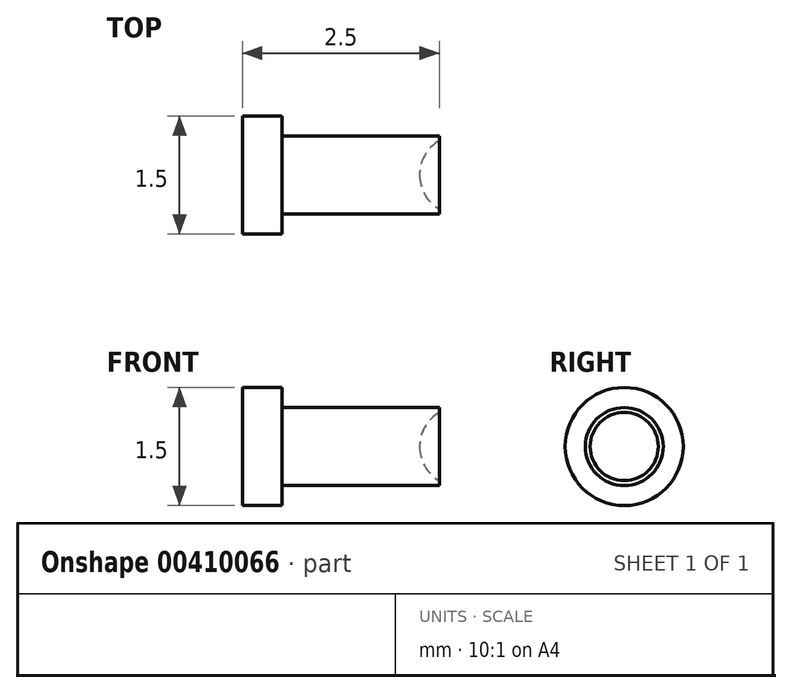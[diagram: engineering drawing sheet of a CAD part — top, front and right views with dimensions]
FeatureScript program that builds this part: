
annotation { "Feature Type Name" : "Feature", "Feature Type Description" : "" }
export const myFeature = defineFeature(function(context is Context, id is Id, definition is map)
    precondition{}
    {
        {
            var Q0;
            Q0=qCreatedBy(makeId("Front.planeOp"),FACE);
            var sketch = newSketch(context, id + "F0", { "sketchPlane" : qUnion([Q0])});
            skLineSegment(sketch, "E0", {"start": v(0, 0) * mm, "end": v(2.5, 0) * mm});
            skLineSegment(sketch, "E1", {"start": v(2.5, 0) * mm, "end": v(2.5, 0.5) * mm});
            skLineSegment(sketch, "E2", {"start": v(2.5, 0.5) * mm, "end": v(0.5, 0.5) * mm});
            skLineSegment(sketch, "E3", {"start": v(0.5, 0.5) * mm, "end": v(0.5, 0.75) * mm});
            skLineSegment(sketch, "E4", {"start": v(0.5, 0.75) * mm, "end": v(0, 0.75) * mm});
            skArc(sketch, "E5", {"start": v(2.5, 0.43) * mm, "mid": v(2.32, 0.25) * mm, "end": v(2.25, 0) * mm});
            skLineSegment(sketch, "E6", {"start": v(0, 0.75) * mm, "end": v(0, 0) * mm});
            skSolve(sketch);
        }
        {
            var Q0;
            {var subQ0=sQuery(id+"F0.wireOp",EDGE,"E2");Q0=makeQuery(id+"F0.imprint","IMPRINT",FACE,{"disambiguationData":[TD([[makeQuery(id+"F0.imprint","IMPRINT",EDGE,{"derivedFrom":subQ0}),1.0]])]});}
            var Q1;
            Q1=sQuery(id+"F0.wireOp",EDGE,"E0");
            revolve(context, id + "F1", {"entities" : qUnion([Q0]), "axis" : qUnion([Q1]), "revolveType" : RevolveType.FULL});
        }
    });
